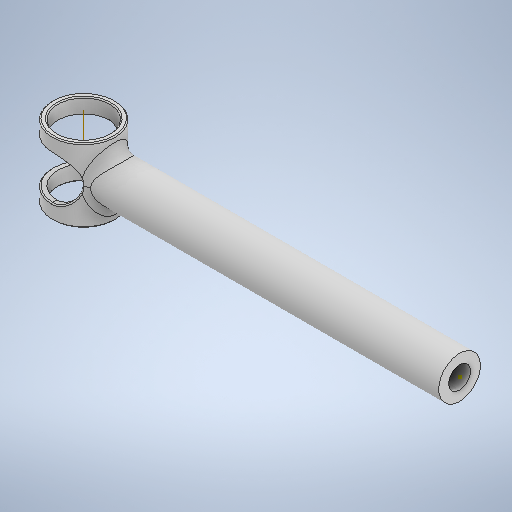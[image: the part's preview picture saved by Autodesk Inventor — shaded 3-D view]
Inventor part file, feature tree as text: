
AUTODESK INVENTOR PART (.ipt)
format: ipt  version: 2025.1 (Build 291241000, 241)  size: 397,824 bytes
history: native  units: mm
features: sketch x6, extrude x4, fillet x2, revolve x1, other x1
ambient origin geometry x8: Origin, YZ Plane, XZ Plane, XY Plane, X Axis, Y Axis, Z Axis, Center Point
bodies: Volumenkörper1 (feature_tree)
feature tree (14):
  revolve  "Umdrehung1"
  extrude  "Extrusion1"  Depth=4.0mm
  fillet  "Rundung1"  [1 undecoded]
  extrude  "Extrusion2"  TaperAngle=90.0deg  [1 undecoded]
  extrude  "Extrusion3"  Depth=14.0mm TaperAngle=0.0deg
  fillet  "Rundung2"  Radius=2.0mm
  sketch  "Skizze5"  dims[d12=4.15mm]
  extrude  "Extrusion4"  Depth=10.0mm TaperAngle=0.0deg
  other  "Arbeitsachse1"
  sketch  "Skizze1"  dims[d0=72.0mm d1=4.0mm d2=0.0mm]
  sketch  "Skizze2"  dims[d3=37.5mm d4=90.0deg]
  sketch  "Skizze3"  dims[d5=12.0mm d6=14.0mm d7=0.0mm d8=2.0mm]
  sketch  "Skizze4"  dims[d9=10.0mm d10=15.0mm d11=0.0mm]
  sketch  "Skizze6"  dims[d13=8.3mm d14=4.15mm d15=1.0mm d16=10.0mm d17=15.0mm d18=0.0mm d19=0.2mm d20=4.2mm d21=4.1mm d22=0.0mm]
note: 2 required parameter values undecoded (feature->parameter linkage not recoverable at this tier; creation-order binding heuristic only, values carry confidence <= 0.55)
